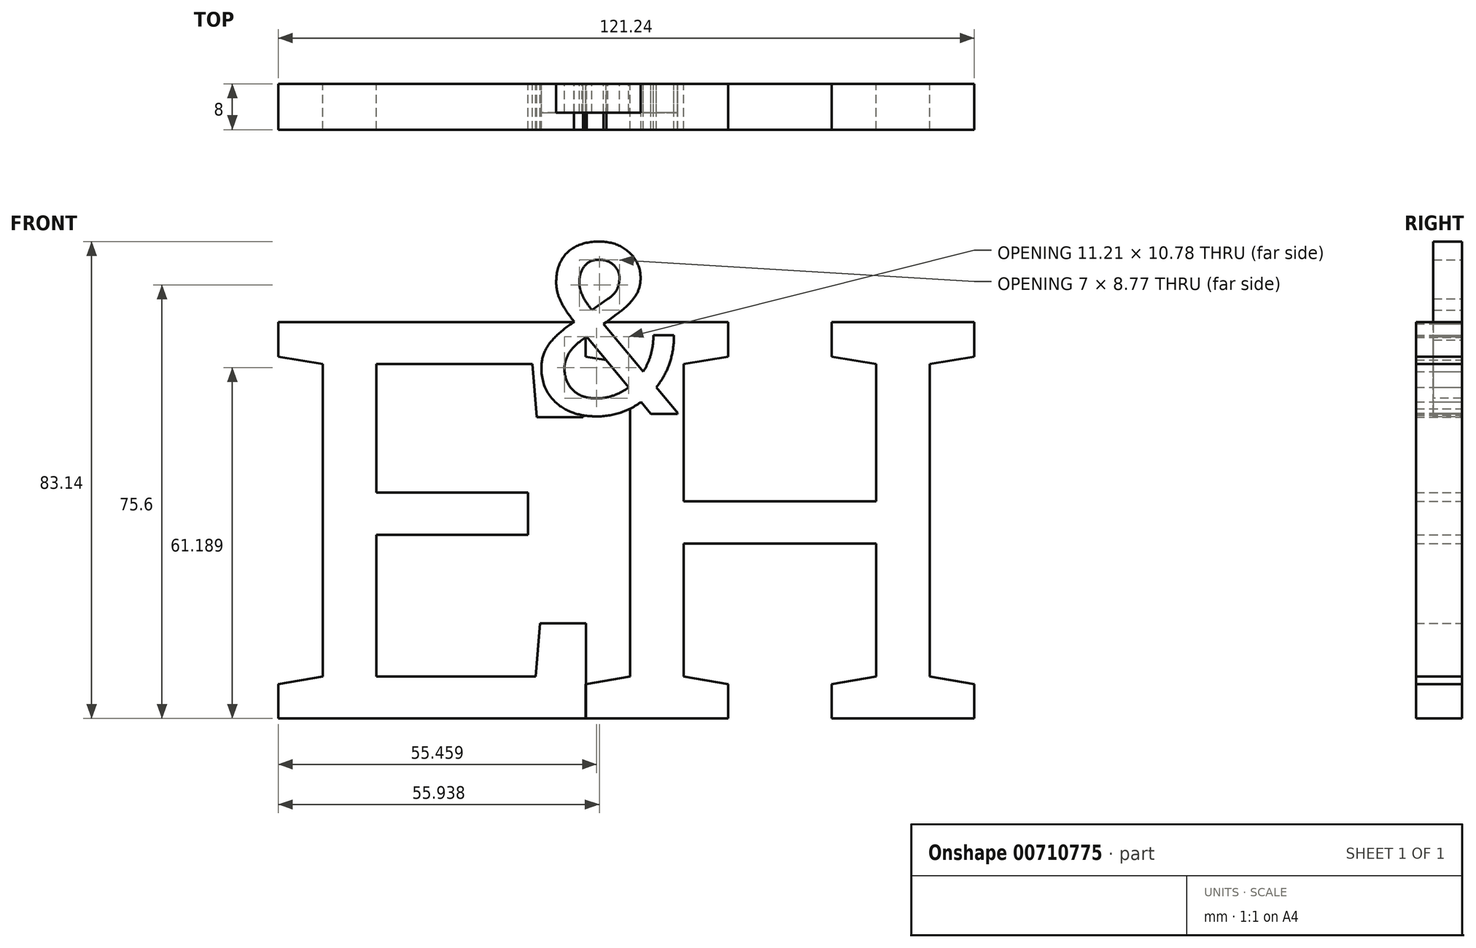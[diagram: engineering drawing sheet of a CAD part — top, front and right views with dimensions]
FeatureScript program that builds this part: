
annotation { "Feature Type Name" : "Feature", "Feature Type Description" : "" }
export const myFeature = defineFeature(function(context is Context, id is Id, definition is map)
    precondition{}
    {
        {
            var Q0;
            Q0=qCreatedBy(makeId("Front.planeOp"),FACE);
            var sketch = newSketch(context, id + "F0", { "sketchPlane" : qUnion([Q0])});
            skText(sketch, "E0", { "text": "E", "fontName": "RobotoSlab-Regular.ttf"});
            skText(sketch, "E1", { "text": "&", "fontName": "RobotoSlab-Regular.ttf"});
            skText(sketch, "E2", { "text": "H", "fontName": "RobotoSlab-Regular.ttf"});
            const initialGuessF0  = {"E0": [-0.28477, 0.08511, 1, 0, 0.07], "E1": [-0.23706, 0.1382, 1, 0, 0.03], "E2": [-0.23122, 0.08511, 1, 0, 0.07]};
            skSetInitialGuess(sketch, initialGuessF0);
            skSolve(sketch);
        }
        {
            var Q0;
            Q0=makeQuery(id+"F0.imprint","IMPRINT",FACE,{"disambiguationData":[TD([[makeQuery(id+"F0.imprint","IMPRINT",EDGE,{"derivedFrom":sQuery(id+"F0.wireOp",EDGE,"E0.sketch_text.stroke-0")}),-1.0]])]});
            var Q1;
            {var subQ0=sQuery(id+"F0.wireOp",EDGE,"E1.sketch_text.stroke-28");var subQ1=sQuery(id+"F0.wireOp",EDGE,"E1.sketch_text.stroke-27");var subQ2=makeQuery(id+"F0.imprint","INTERSECT",VERTEX,{"derivedFrom":[subQ1,subQ0]});Q1=makeQuery(id+"F0.imprint","IMPRINT",FACE,{"disambiguationData":[TD([[makeQuery(id+"F0.imprint","IMPRINT",EDGE,{"disambiguationData":[TD([[subQ2,1.0]])],"derivedFrom":subQ1}),1.0]])]});}
            var Q2;
            {var subQ8=sQuery(id+"F0.wireOp",EDGE,"E1.sketch_text.stroke-11");Q2=makeQuery(id+"F0.imprint","IMPRINT",FACE,{"disambiguationData":[TD([[makeQuery(id+"F0.imprint","IMPRINT",EDGE,{"derivedFrom":subQ8}),1.0]])]});}
            extrude(context, id + "F1", {"entities" : qUnion([Q0, Q1, Q2]), "depth" : 8 * mm, "offsetDistance" : 25 * mm});
        }
        {
            var Q0;
            {var subQ9=sQuery(id+"F0.wireOp",EDGE,"E1.sketch_text.stroke-2");Q0=makeQuery(id+"F0.imprint","IMPRINT",FACE,{"disambiguationData":[TD([[makeQuery(id+"F0.imprint","IMPRINT",EDGE,{"derivedFrom":subQ9}),-1.0]])]});}
            var Q1;
            {var subQ11=sQuery(id+"F0.wireOp",EDGE,"E1.sketch_text.stroke-0");Q1=makeQuery(id+"F0.imprint","IMPRINT",FACE,{"disambiguationData":[TD([[makeQuery(id+"F0.imprint","IMPRINT",EDGE,{"derivedFrom":subQ11}),-1.0]])]});}
            var Q2;
            {var subQ1=sQuery(id+"F0.wireOp",EDGE,"E1.sketch_text.stroke-22");Q2=makeQuery(id+"F0.imprint","IMPRINT",FACE,{"disambiguationData":[TD([[makeQuery(id+"F0.imprint","IMPRINT",EDGE,{"derivedFrom":subQ1}),-1.0]])]});}
            var Q3;
            {var subQ0=sQuery(id+"F0.wireOp",EDGE,"E1.sketch_text.stroke-11");Q3=makeQuery(id+"F0.imprint","IMPRINT",FACE,{"disambiguationData":[TD([[makeQuery(id+"F0.imprint","IMPRINT",EDGE,{"derivedFrom":subQ0}),-1.0]])]});}
            extrude(context, id + "F2", {"entities" : qUnion([Q0, Q1, Q2, Q3]), "depth" : 5 * mm, "offsetDistance" : 25 * mm});
        }
    });
